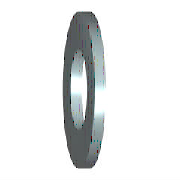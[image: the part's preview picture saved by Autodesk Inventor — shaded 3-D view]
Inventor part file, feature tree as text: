
AUTODESK INVENTOR PART (.ipt)
format: ipt  version: 2014 SP1 (Build 180222100, 222)  size: 104,960 bytes
history: native  units: mm (DEFAULTED — no unit token found)
features: other x1, plane x1, sketch x1
ambient origin geometry x7: Origin, YZ Plane, XY Plane, X Axis, Y Axis, Z Axis, Center Point
bodies: Solid1 (feature_tree), Body (feature_tree)
feature tree (3):
  other  "Work Axis1"
  plane  "Work Plane1"
  sketch  "Sketch"  dims[d0=7.1374mm d1=15.875mm d2=2.032mm d3=0.0mm d4=0.0mm d5=0.0mm d6=0.0mm d7=0.0mm]
